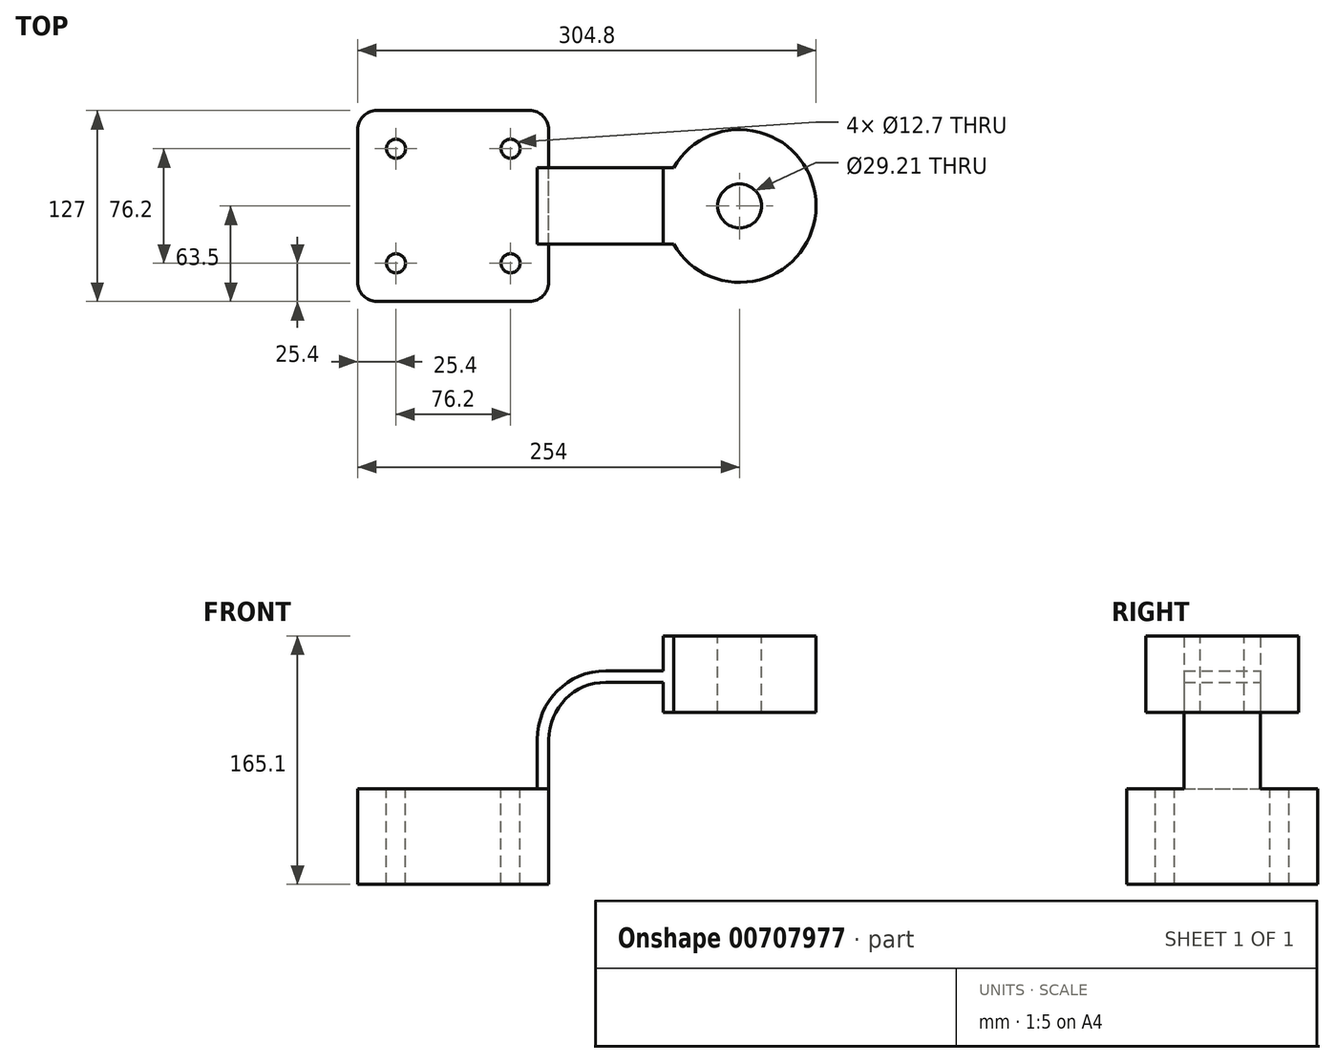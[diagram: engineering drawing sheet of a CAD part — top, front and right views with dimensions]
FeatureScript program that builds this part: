
annotation { "Feature Type Name" : "Feature", "Feature Type Description" : "" }
export const myFeature = defineFeature(function(context is Context, id is Id, definition is map)
    precondition{}
    {
        {
            var Q0;
            Q0=qCreatedBy(makeId("Front.planeOp"),FACE);
            var sketch = newSketch(context, id + "F0", { "sketchPlane" : qUnion([Q0])});
            skLineSegment(sketch, "E0.bottom", {"start": v(-63.5, 31.75) * mm, "end": v(63.5, 31.75) * mm});
            skLineSegment(sketch, "E0.top", {"start": v(-63.5, -31.75) * mm, "end": v(63.5, -31.75) * mm});
            skLineSegment(sketch, "E0.left", {"start": v(-63.5, 31.75) * mm, "end": v(-63.5, -31.75) * mm});
            skLineSegment(sketch, "E0.right", {"start": v(63.5, 31.75) * mm, "end": v(63.5, -31.75) * mm});
            skPoint(sketch, "E0.middle", {"position": v(0, 0) * mm});
            skLineSegment(sketch, "E1.bottom", {"start": v(139.7, 133.35) * mm, "end": v(241.3, 133.35) * mm});
            skLineSegment(sketch, "E1.top", {"start": v(139.7, 82.55) * mm, "end": v(241.3, 82.55) * mm});
            skLineSegment(sketch, "E1.left", {"start": v(139.7, 133.35) * mm, "end": v(139.7, 82.55) * mm});
            skLineSegment(sketch, "E1.right", {"start": v(241.3, 133.35) * mm, "end": v(241.3, 82.55) * mm});
            skPoint(sketch, "E1.middle", {"position": v(190.5, 107.95) * mm});
            skLineSegment(sketch, "E2", {"start": v(63.5, 31.75) * mm, "end": v(63.5, 64.46) * mm});
            skArc(sketch, "E3", {"start": v(63.5, 64.46) * mm, "mid": v(74.66, 91.4) * mm, "end": v(101.6, 102.56) * mm});
            skLineSegment(sketch, "E4", {"start": v(101.6, 102.56) * mm, "end": v(163.3, 102.56) * mm});
            skLineSegment(sketch, "E5.0", {"start": v(101.6, 110.18) * mm, "end": v(163.3, 110.18) * mm});
            skArc(sketch, "E5.1", {"start": v(55.88, 64.46) * mm, "mid": v(69.27, 96.8) * mm, "end": v(101.6, 110.18) * mm});
            skLineSegment(sketch, "E5.2", {"start": v(55.88, 31.75) * mm, "end": v(55.88, 64.46) * mm});
            skFitSpline(sketch, "E6", {"points": [v(-63.5, 31.75) * mm, v(101.6, 110.18) * mm], "startDerivative": vector(66.65, 190.5) * mm, "endDerivative": vector(213.01, -1.29) * mm});
            skLineSegment(sketch, "E7", {"start": v(190.5, 82.55) * mm, "end": v(190.5, 133.35) * mm});
            skSolve(sketch);
        }
        {
            var Q0;
            Q0=makeQuery(id+"F0.imprint","IMPRINT",FACE,{"disambiguationData":[TD([[makeQuery(id+"F0.imprint","IMPRINT",EDGE,{"derivedFrom":sQuery(id+"F0.wireOp",EDGE,"E0.top")}),1.0]])]});
            extrude(context, id + "F1", {"entities" : qUnion([Q0]), "endBound" : BoundingType.SYMMETRIC, "depth" : 127 * mm, "offsetDistance" : 25.4 * mm});
        }
        {
            var Q0;
            {var subQ4=sQuery(id+"F0.wireOp",EDGE,"E7");Q0=makeQuery(id+"F0.imprint","IMPRINT",FACE,{"disambiguationData":[TD([[makeQuery(id+"F0.imprint","IMPRINT",EDGE,{"derivedFrom":subQ4}),1.0]])]});}
            var Q1;
            {var subQ1=sQuery(id+"F0.wireOp",EDGE,"E2");Q1=makeQuery(id+"F0.imprint","IMPRINT",FACE,{"disambiguationData":[TD([[makeQuery(id+"F0.imprint","IMPRINT",EDGE,{"derivedFrom":subQ1}),1.0]])]});}
            extrude(context, id + "F2", {"entities" : qUnion([Q0, Q1]), "operationType" : NewBodyOperationType.ADD, "endBound" : BoundingType.SYMMETRIC, "depth" : 50.8 * mm, "offsetDistance" : 25.4 * mm});
        }
        {
            var Q0;
            Q0=makeQuery(id+"F0.imprint","IMPRINT",FACE,{"disambiguationData":[TD([[makeQuery(id+"F0.imprint","IMPRINT",EDGE,{"derivedFrom":sQuery(id+"F0.wireOp",EDGE,"E5.1")}),1.0]])]});
            extrude(context, id + "F3", {"entities" : qUnion([Q0]), "operationType" : NewBodyOperationType.ADD, "endBound" : BoundingType.SYMMETRIC, "depth" : 12.7 * mm, "offsetDistance" : 25.4 * mm});
        }
        {
            var Q0;
            {var subQ0=sQuery(id+"F0.wireOp",EDGE,"E1.right");Q0=makeQuery(id+"F0.imprint","IMPRINT",FACE,{"disambiguationData":[TD([[makeQuery(id+"F0.imprint","IMPRINT",EDGE,{"derivedFrom":subQ0}),-1.0]])]});}
            var Q1;
            Q1=sQuery(id+"F0.wireOp",EDGE,"E7");
            revolve(context, id + "F4", {"operationType" : NewBodyOperationType.ADD, "entities" : qUnion([Q0]), "axis" : qUnion([Q1]), "revolveType" : RevolveType.FULL});
        }
        {
            var Q0;
            Q0=makeQuery(id+"F1.opExtrude","CAP_EDGE",EDGE,{"disambiguationData":[OSD([sQuery(id+"F0.wireOp",EDGE,"E0.right")])],"isStart":false});
            var Q1;
            Q1=makeQuery(id+"F1.opExtrude","CAP_EDGE",EDGE,{"disambiguationData":[OSD([sQuery(id+"F0.wireOp",EDGE,"E0.left")])],"isStart":false});
            var Q2;
            Q2=makeQuery(id+"F1.opExtrude","CAP_EDGE",EDGE,{"disambiguationData":[OSD([sQuery(id+"F0.wireOp",EDGE,"E0.left")])],"isStart":true});
            var Q3;
            Q3=makeQuery(id+"F1.opExtrude","CAP_EDGE",EDGE,{"disambiguationData":[OSD([sQuery(id+"F0.wireOp",EDGE,"E0.right")])],"isStart":true});
            fillet(context, id + "F5", {"entities" : qUnion([Q0, Q1, Q2, Q3]), "radius" : 12.7 * mm, "tangentPropagation" : true, "allowEdgeOverflow" : false});
        }
        {
            var Q0;
            {var subQ0=sQuery(id+"F0.wireOp",EDGE,"E1.bottom");Q0=makeQuery(id+"F4.boolean.opBoolean","MERGE",FACE,{"derivedFrom":[makeQuery(id+"F2.opExtrude","SWEPT_FACE",FACE,{"disambiguationData":[OSD([subQ0])]}),makeQuery(id+"F4.opRevolve","SWEPT_FACE",FACE,{"disambiguationData":[OSD([subQ0])]})]});}
            var sketch = newSketch(context, id + "F6", { "sketchPlane" : qUnion([Q0])});
            skCircle(sketch, "E8", {"center": v(190.5, 0) * mm, "radius": 14.6 * mm});
            skSolve(sketch);
        }
        {
            var Q0;
            Q0 = qSketchRegion(id + "F6", true);
            extrude(context, id + "F7", {"entities" : qUnion([Q0]), "operationType" : NewBodyOperationType.REMOVE, "endBound" : BoundingType.THROUGH_ALL, "oppositeDirection" : true, "depth" : 25.4 * mm, "offsetDistance" : 25.4 * mm});
        }
        {
            var Q0;
            {var subQ3=sQuery(id+"F0.wireOp",EDGE,"E0.bottom");var subQ5=sQuery(id+"F0.wireOp",EDGE,"E0.right");var subQ6=sQuery(id+"F0.wireOp",EDGE,"E0.left");Q0=makeQuery(id+"F3.boolean.opBoolean","SPLIT",FACE,{"disambiguationData":[TD([makeQuery(id+"F1.opExtrude","CAP_FACE",FACE,{"disambiguationData":[OSD([subQ3,sQuery(id+"F0.wireOp",EDGE,"E0.top"),subQ6,subQ5])],"isStart":false})])],"derivedFrom":makeQuery(id+"F1.opExtrude","SWEPT_FACE",FACE,{"disambiguationData":[OSD([subQ3])]})});}
            var sketch = newSketch(context, id + "F8", { "sketchPlane" : qUnion([Q0])});
            skCircle(sketch, "E9", {"center": v(-38.1, -38.1) * mm, "radius": 6.35 * mm});
            skCircle(sketch, "E10", {"center": v(38.1, -38.1) * mm, "radius": 6.35 * mm});
            skCircle(sketch, "E11", {"center": v(38.1, 38.1) * mm, "radius": 6.35 * mm});
            skCircle(sketch, "E12", {"center": v(-38.1, 38.1) * mm, "radius": 6.35 * mm});
            skSolve(sketch);
        }
        {
            var Q0;
            Q0=makeQuery(id+"F8.imprint","IMPRINT",FACE,{"disambiguationData":[TD([[makeQuery(id+"F8.imprint","IMPRINT",EDGE,{"derivedFrom":sQuery(id+"F8.wireOp",EDGE,"E9")}),1.0]])]});
            var Q1;
            Q1=makeQuery(id+"F8.imprint","IMPRINT",FACE,{"disambiguationData":[TD([[makeQuery(id+"F8.imprint","IMPRINT",EDGE,{"derivedFrom":sQuery(id+"F8.wireOp",EDGE,"E10")}),1.0]])]});
            var Q2;
            Q2=makeQuery(id+"F8.imprint","IMPRINT",FACE,{"disambiguationData":[TD([[makeQuery(id+"F8.imprint","IMPRINT",EDGE,{"derivedFrom":sQuery(id+"F8.wireOp",EDGE,"E11")}),1.0]])]});
            var Q3;
            Q3=makeQuery(id+"F8.imprint","IMPRINT",FACE,{"disambiguationData":[TD([[makeQuery(id+"F8.imprint","IMPRINT",EDGE,{"derivedFrom":sQuery(id+"F8.wireOp",EDGE,"E12")}),1.0]])]});
            extrude(context, id + "F9", {"entities" : qUnion([Q0, Q1, Q2, Q3]), "operationType" : NewBodyOperationType.REMOVE, "endBound" : BoundingType.THROUGH_ALL, "oppositeDirection" : true, "depth" : 25.4 * mm, "offsetDistance" : 25.4 * mm});
        }
    });
